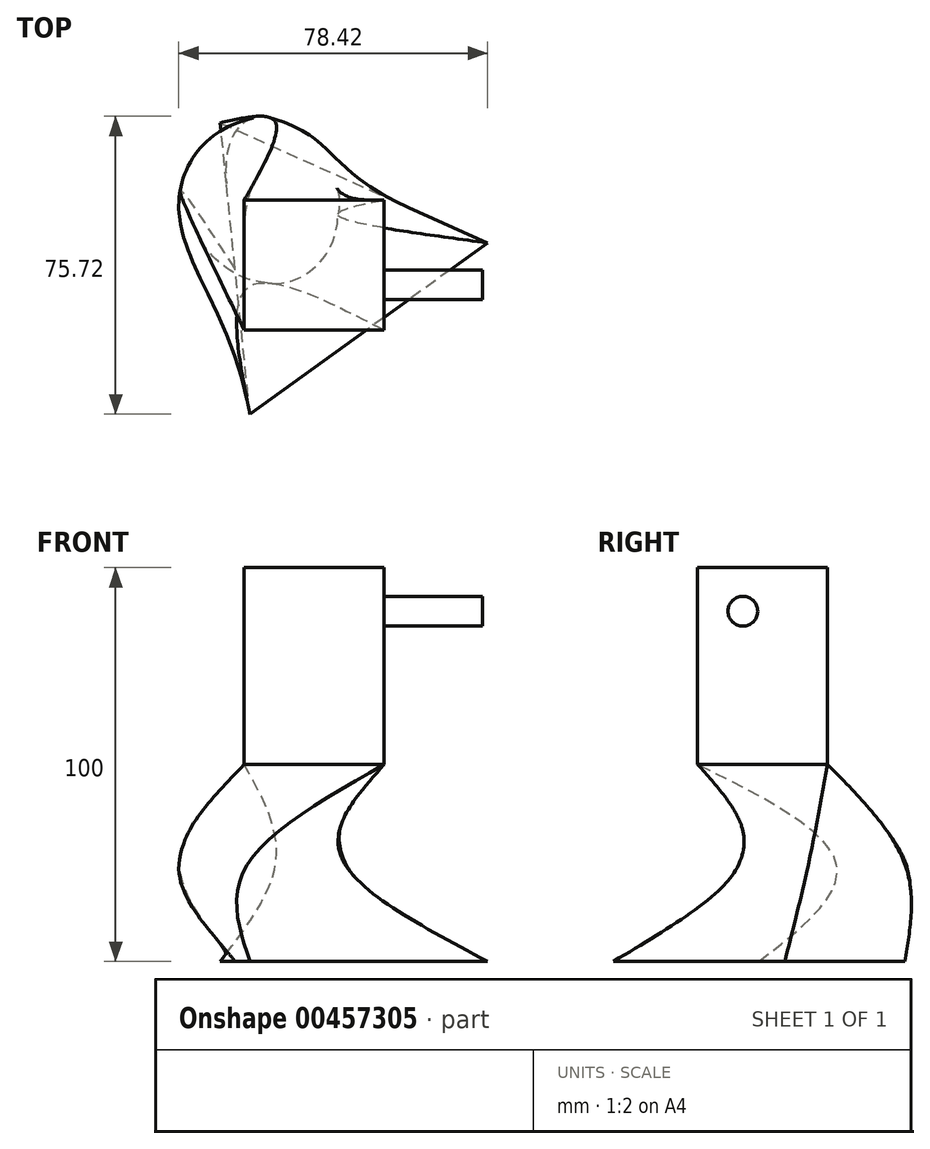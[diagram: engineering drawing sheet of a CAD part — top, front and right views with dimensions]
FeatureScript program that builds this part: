
annotation { "Feature Type Name" : "Feature", "Feature Type Description" : "" }
export const myFeature = defineFeature(function(context is Context, id is Id, definition is map)
    precondition{}
    {
        {
            var Q0;
            Q0=qCreatedBy(makeId("Top.planeOp"),FACE);
            var sketch = newSketch(context, id + "F0", { "sketchPlane" : qUnion([Q0])});
            skCircle(sketch, "E0.cCircle", {"center": v(0, 0) * mm, "radius": 21.48 * mm, "construction": true});
            skLineSegment(sketch, "E0.0", {"start": v(42.74, 4.34) * mm, "end": v(-17.6, -39.18) * mm});
            skLineSegment(sketch, "E0.1", {"start": v(-17.6, -39.18) * mm, "end": v(-25.13, 34.84) * mm});
            skLineSegment(sketch, "E0.2", {"start": v(-25.13, 34.84) * mm, "end": v(42.74, 4.34) * mm});
            skPoint(sketch, "E0.0.midPoint", {"position": v(12.57, -17.42) * mm});
            skSolve(sketch);
        }
        {
            var Q0;
            Q0=qCreatedBy(makeId("Top.planeOp"),FACE);
            cPlane(context, id + "F1", {"entities" : qUnion([Q0]), "cplaneType" : CPlaneType.OFFSET, "offset" : 25 * mm, "width" : 150 * mm, "height" : 150 * mm});
        }
        {
            var Q0;
            Q0=qCreatedBy(id+"F1.planeOp",FACE);
            var sketch = newSketch(context, id + "F2", { "sketchPlane" : qUnion([Q0])});
            skCircle(sketch, "E1", {"center": v(-14.52, 13.93) * mm, "radius": 21.12 * mm});
            skSolve(sketch);
        }
        {
            var Q0;
            Q0=qCreatedBy(id+"F1.planeOp",FACE);
            cPlane(context, id + "F3", {"entities" : qUnion([Q0]), "cplaneType" : CPlaneType.OFFSET, "offset" : 25 * mm, "width" : 150 * mm, "height" : 150 * mm});
        }
        {
            var Q0;
            Q0=qCreatedBy(id+"F3.planeOp",FACE);
            var sketch = newSketch(context, id + "F4", { "sketchPlane" : qUnion([Q0])});
            skLineSegment(sketch, "E2.bottom", {"start": v(-19.05, 15.24) * mm, "end": v(16.51, 15.24) * mm});
            skLineSegment(sketch, "E2.top", {"start": v(-19.05, -17.78) * mm, "end": v(16.51, -17.78) * mm});
            skLineSegment(sketch, "E2.left", {"start": v(-19.05, 15.24) * mm, "end": v(-19.05, -17.78) * mm});
            skLineSegment(sketch, "E2.right", {"start": v(16.51, 15.24) * mm, "end": v(16.51, -17.78) * mm});
            skSolve(sketch);
        }
        {
            var Q0;
            Q0=makeQuery(id+"F0.imprint","IMPRINT",FACE,{"disambiguationData":[TD([[makeQuery(id+"F0.imprint","IMPRINT",EDGE,{"derivedFrom":sQuery(id+"F0.wireOp",EDGE,"E0.0")}),-1.0]])]});
            var Q1;
            Q1=makeQuery(id+"F2.imprint","IMPRINT",FACE,{"disambiguationData":[TD([[makeQuery(id+"F2.imprint","IMPRINT",EDGE,{"derivedFrom":sQuery(id+"F2.wireOp",EDGE,"E1")}),1.0]])]});
            var Q2;
            Q2=makeQuery(id+"F4.imprint","IMPRINT",FACE,{"disambiguationData":[TD([[makeQuery(id+"F4.imprint","IMPRINT",EDGE,{"derivedFrom":sQuery(id+"F4.wireOp",EDGE,"E2.bottom")}),-1.0]])]});
            loft(context, id + "F5", {"sheetProfilesArray" : [{ "sheetProfileEntities" : qUnion([Q0]) }, { "sheetProfileEntities" : qUnion([Q1]) }, { "sheetProfileEntities" : qUnion([Q2]) }]});
        }
        {
            var Q0;
            Q0=makeQuery(id+"F5.opLoft","CAP_FACE",FACE,{"disambiguationData":[OSD([makeQuery(id+"F4.imprint","IMPRINT",FACE,{"disambiguationData":[TD([[makeQuery(id+"F4.imprint","IMPRINT",EDGE,{"derivedFrom":sQuery(id+"F4.wireOp",EDGE,"E2.bottom")}),-1.0]])]})])],"isStart":true});
            extrude(context, id + "F6", {"entities" : qUnion([Q0]), "operationType" : NewBodyOperationType.ADD, "depth" : 50 * mm});
        }
        {
            var Q0;
            Q0=makeQuery(id+"F6.opExtrude","SWEPT_FACE",FACE,{"disambiguationData":[OSD([sQuery(id+"F4.wireOp",EDGE,"E2.bottom"),sQuery(id+"F4.wireOp",EDGE,"E2.top"),sQuery(id+"F4.wireOp",EDGE,"E2.right")])]});
            var sketch = newSketch(context, id + "F7", { "sketchPlane" : qUnion([Q0])});
            skCircle(sketch, "E3", {"center": v(-6.29, 88.95) * mm, "radius": 3.78 * mm});
            skSolve(sketch);
        }
        {
            var Q0;
            Q0 = qSketchRegion(id + "F7", true);
            extrude(context, id + "F8", {"entities" : qUnion([Q0]), "operationType" : NewBodyOperationType.ADD, "depth" : 25 * mm});
        }
    });
